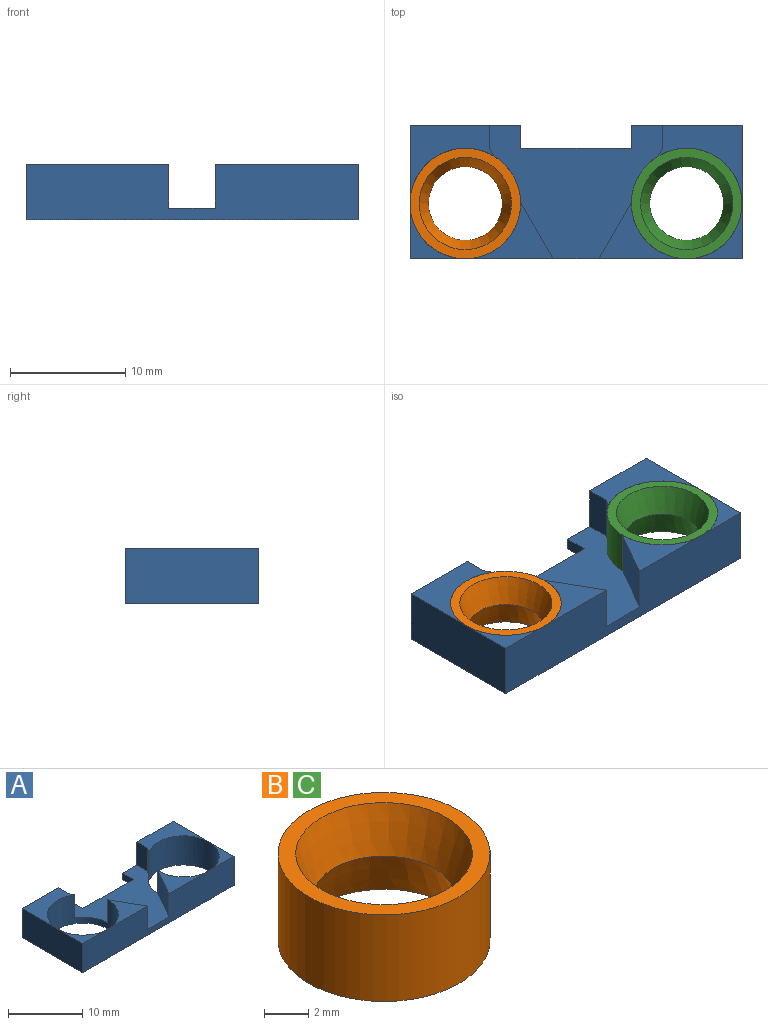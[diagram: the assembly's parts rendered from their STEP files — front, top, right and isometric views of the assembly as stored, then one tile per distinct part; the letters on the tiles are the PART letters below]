
ASSEMBLY  parts=3 mates=2
PART A: 20 faces, bbox 28.8x11.6x4.8 mm
  f0: plane 15x11.6mm, normal (0,0,1), area 98.3mm2, adj f1,f2,f3,f5,f7,f8,f9,f10
  f1: plane 9.6x1mm, normal (0,1,0), area 9.6mm2, adj f0,f2,f9,f11
  f2: plane 2x1mm, normal (1,0,0), area 2mm2, adj f0,f1,f3,f11
  f3: plane 9.6x4.8mm, normal (0,1,0), area 35.8mm2, adj f0,f2,f4,f11,f17,f19
  f4: plane 11.6x4.8mm, normal (-1,0,0), area 55.7mm2, adj f3,f5,f11,f19
  f5: plane 28.8x4.8mm, normal (0,-1,0), area 123mm2, adj f0,f4,f6,f11,f14,f15,f18,f19
  f6: plane 11.6x4.8mm, normal (1,0,0), area 55.7mm2, adj f5,f7,f11,f15
  f7: plane 9.6x4.8mm, normal (0,1,0), area 35.8mm2, adj f0,f6,f9,f11,f12,f15
  f8: cylinder r=4.8mm len=9.6mm, axis (0,0,-1), area 126.5mm2, adj f0,f11,f13,f14,f15
  f9: plane 2x1mm, normal (-1,0,0), area 2mm2, adj f0,f1,f7,f11
  f10: cylinder r=4.8mm len=9.6mm, axis (0,0,-1), area 126.5mm2, adj f0,f11,f16,f18,f19
  f11: plane 28.8x11.6mm, normal (0,0,-1), area 170.1mm2, adj f1,f2,f3,f4,f5,f6,f7,f8
  f12: plane 3.8x2mm, normal (-1,0,0), area 7.6mm2, adj f0,f7,f13,f15
  f13: plane 3.8x0.71mm, normal (-0.87,0.5,0), area 3.1mm2, adj f0,f8,f12,f15
  f14: plane 4.89x3.8mm, normal (-0.87,0.5,0), area 21.4mm2, adj f0,f5,f8,f15
  f15: plane 12.4x11.6mm, normal (0,0,1), area 35.9mm2, adj f5,f6,f7,f8,f12,f13,f14
  f16: plane 3.8x0.71mm, normal (0.87,0.5,0), area 3.1mm2, adj f0,f10,f17,f19
  f17: plane 3.8x2mm, normal (1,0,0), area 7.6mm2, adj f0,f3,f16,f19
  f18: plane 4.89x3.8mm, normal (0.87,0.5,0), area 21.4mm2, adj f0,f5,f10,f19
  f19: plane 12.4x11.6mm, normal (0,0,1), area 35.9mm2, adj f3,f4,f5,f10,f16,f17,f18
PART B: 5 faces, bbox 9.6x9.6x4.8 mm
  f0: cylinder r=4.8mm len=9.6mm, axis (0,0,-1), area 144.8mm2, adj f1,f2
  f1: plane 9.6x9.6mm, normal (0,0,1), area 22.1mm2, adj f0,f3
  f2: plane 9.6x9.6mm, normal (0,0,-1), area 22.1mm2, adj f0,f4
  f3: cone r=3.2mm half-angle=18.4deg, axis (0,0,1), area 57.2mm2, adj f1,f4
  f4: cone r=4mm half-angle=18.4deg, axis (0,0,-1), area 57.2mm2, adj f2,f3
PART C: same geometry as B
PLACE A t=(-29.69,4.08,-1.7)mm
PLACE B t=(-0.73,5.59,-1.7)mm
PLACE C t=(18.47,5.59,-1.7)mm
MATE fastened B.f0 <-> A.f10  axis (0,0,-1) through (-0.73,5.59,-1.7)mm
MATE fastened C.f0 <-> A.f8  axis (0,0,-1) through (18.47,5.59,-1.7)mm
